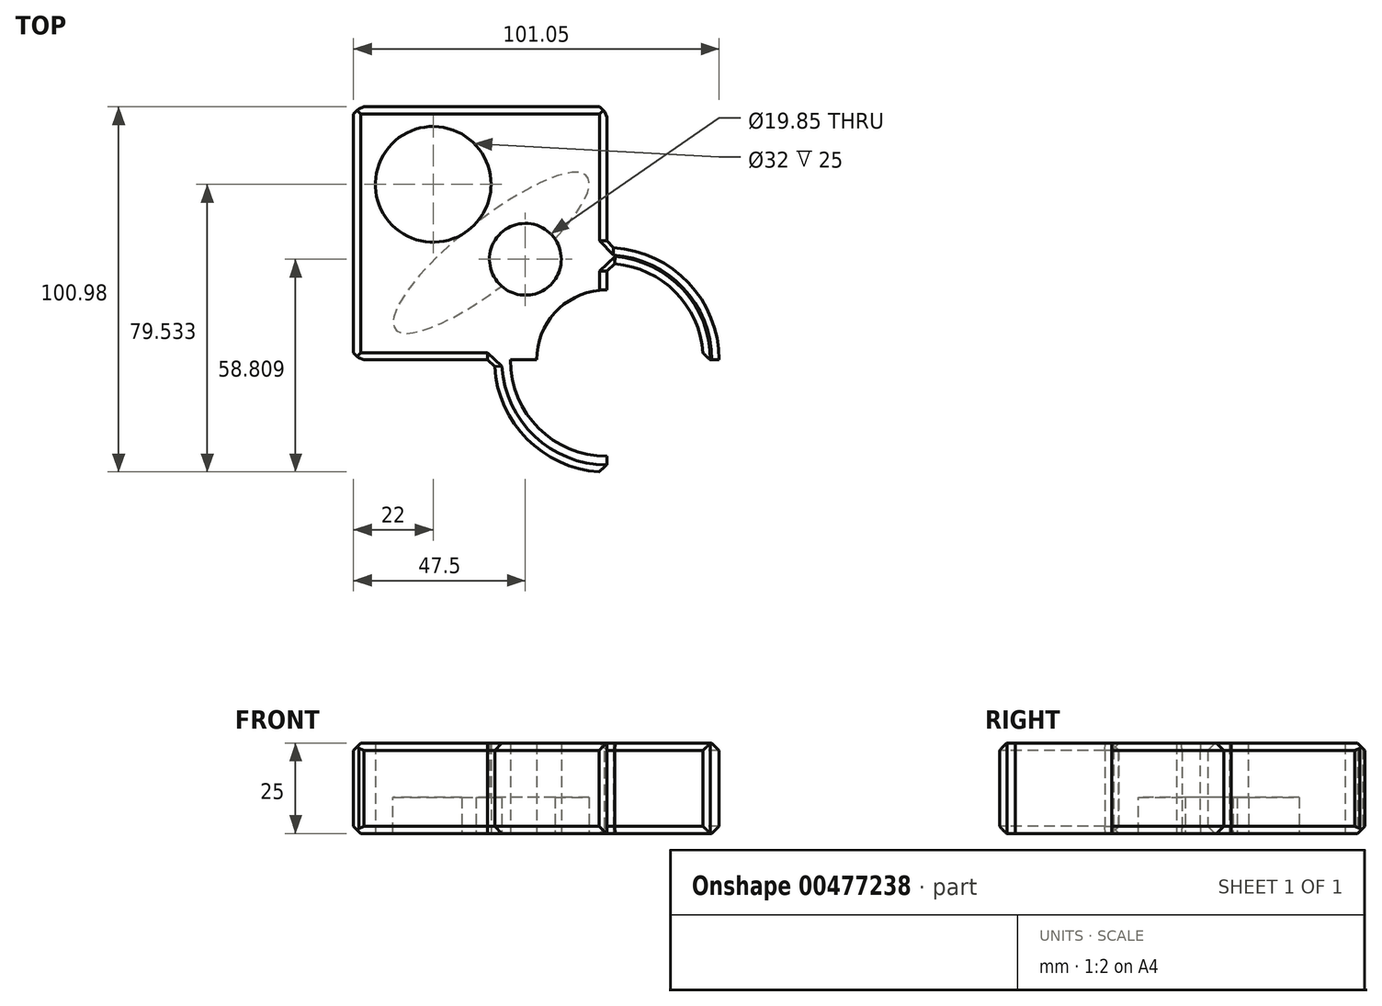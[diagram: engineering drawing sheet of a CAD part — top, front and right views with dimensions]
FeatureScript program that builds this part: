
annotation { "Feature Type Name" : "Feature", "Feature Type Description" : "" }
export const myFeature = defineFeature(function(context is Context, id is Id, definition is map)
    precondition{}
    {
        {
            var Q0;
            Q0=qCreatedBy(makeId("Top.planeOp"),FACE);
            var sketch = newSketch(context, id + "F0", { "sketchPlane" : qUnion([Q0])});
            skCircle(sketch, "E0", {"center": v(0, 0) * mm, "radius": 31.05 * mm});
            skSolve(sketch);
        }
        {
            var Q0;
            Q0=makeQuery(id+"F0.imprint","IMPRINT",FACE,{"disambiguationData":[TD([[makeQuery(id+"F0.imprint","IMPRINT",EDGE,{"derivedFrom":sQuery(id+"F0.wireOp",EDGE,"E0")}),1.0]])]});
            extrude(context, id + "F1", {"entities" : qUnion([Q0]), "depth" : 25 * mm});
        }
        {
            var Q0;
            Q0=qCreatedBy(makeId("Top.planeOp"),FACE);
            var sketch = newSketch(context, id + "F2", { "sketchPlane" : qUnion([Q0])});
            skCircle(sketch, "E1", {"center": v(0, 0) * mm, "radius": 26.67 * mm});
            skSolve(sketch);
        }
        {
            var Q0;
            Q0=makeQuery(id+"F2.imprint","IMPRINT",FACE,{"disambiguationData":[TD([[makeQuery(id+"F2.imprint","IMPRINT",EDGE,{"derivedFrom":sQuery(id+"F2.wireOp",EDGE,"E1")}),1.0]])]});
            extrude(context, id + "F3", {"entities" : qUnion([Q0]), "operationType" : NewBodyOperationType.REMOVE, "depth" : 25.2 * mm});
        }
        {
            var Q0;
            Q0=qCreatedBy(makeId("Top.planeOp"),FACE);
            var sketch = newSketch(context, id + "F4", { "sketchPlane" : qUnion([Q0])});
            skLineSegment(sketch, "E2.bottom", {"start": v(0, 0) * mm, "end": v(-70, 0) * mm});
            skLineSegment(sketch, "E2.top", {"start": v(0, 70) * mm, "end": v(-70, 70) * mm});
            skLineSegment(sketch, "E2.left", {"start": v(0, 0) * mm, "end": v(0, 70) * mm});
            skLineSegment(sketch, "E2.right", {"start": v(-70, 0) * mm, "end": v(-70, 70) * mm});
            skSolve(sketch);
        }
        {
            var Q0;
            Q0=qCreatedBy(makeId("Top.planeOp"),FACE);
            var sketch = newSketch(context, id + "F5", { "sketchPlane" : qUnion([Q0])});
            skLineSegment(sketch, "E3.bottom", {"start": v(70, -70) * mm, "end": v(0, -70) * mm});
            skLineSegment(sketch, "E3.top", {"start": v(70, 0) * mm, "end": v(0, 0) * mm});
            skLineSegment(sketch, "E3.left", {"start": v(70, -70) * mm, "end": v(70, 0) * mm});
            skLineSegment(sketch, "E3.right", {"start": v(0, -70) * mm, "end": v(0, 0) * mm});
            skSolve(sketch);
        }
        {
            var Q0;
            Q0=makeQuery(id+"F4.imprint","IMPRINT",FACE,{"disambiguationData":[TD([[makeQuery(id+"F4.imprint","IMPRINT",EDGE,{"derivedFrom":sQuery(id+"F4.wireOp",EDGE,"E2.bottom")}),-1.0]])]});
            extrude(context, id + "F6", {"entities" : qUnion([Q0]), "operationType" : NewBodyOperationType.ADD, "depth" : 25 * mm});
        }
        {
            var Q0;
            Q0=makeQuery(id+"F5.imprint","IMPRINT",FACE,{"disambiguationData":[TD([[makeQuery(id+"F5.imprint","IMPRINT",EDGE,{"derivedFrom":sQuery(id+"F5.wireOp",EDGE,"E3.bottom")}),-1.0]])]});
            extrude(context, id + "F7", {"entities" : qUnion([Q0]), "operationType" : NewBodyOperationType.REMOVE, "depth" : 25 * mm});
        }
        {
            var Q0;
            Q0=qCreatedBy(makeId("Top.planeOp"),FACE);
            var sketch = newSketch(context, id + "F8", { "sketchPlane" : qUnion([Q0])});
            skCircle(sketch, "E4", {"center": v(0, 0) * mm, "radius": 19.4 * mm});
            skSolve(sketch);
        }
        {
            var Q0;
            Q0 = qSketchRegion(id + "F8", true);
            extrude(context, id + "F9", {"entities" : qUnion([Q0]), "operationType" : NewBodyOperationType.REMOVE, "endBound" : BoundingType.THROUGH_ALL, "depth" : 25 * mm});
        }
        {
            var Q0;
            Q0=qCreatedBy(makeId("Top.planeOp"),FACE);
            var sketch = newSketch(context, id + "F10", { "sketchPlane" : qUnion([Q0])});
            skEllipse(sketch, "E5", {"center": v(-31.97, 29.6) * mm, "majorRadius": 33.9 * mm, "minorRadius": 9.04 * mm, "majorAxis": v(0.78, 0.62)});
            skSolve(sketch);
        }
        {
            var Q0;
            Q0 = qSketchRegion(id + "F10", true);
            extrude(context, id + "F11", {"entities" : qUnion([Q0]), "operationType" : NewBodyOperationType.REMOVE, "depth" : 10 * mm});
        }
        {
            var Q0;
            Q0=qCreatedBy(makeId("Top.planeOp"),FACE);
            var sketch = newSketch(context, id + "F12", { "sketchPlane" : qUnion([Q0])});
            skCircle(sketch, "E6", {"center": v(-22.5, 27.83) * mm, "radius": 9.93 * mm});
            skSolve(sketch);
        }
        {
            var Q0;
            Q0=makeQuery(id+"F12.imprint","IMPRINT",FACE,{"disambiguationData":[TD([[makeQuery(id+"F12.imprint","IMPRINT",EDGE,{"derivedFrom":sQuery(id+"F12.wireOp",EDGE,"E6")}),1.0]])]});
            var Q1;
            Q1=sQuery(id+"F12.wireOp",EDGE,"E6");
            extrude(context, id + "F13", {"entities" : qUnion([Q0]), "operationType" : NewBodyOperationType.REMOVE, "surfaceEntities" : qUnion([Q1]), "endBound" : BoundingType.THROUGH_ALL, "depth" : 25 * mm});
        }
        {
            var Q0;
            Q0=qCreatedBy(makeId("Top.planeOp"),FACE);
            var sketch = newSketch(context, id + "F14", { "sketchPlane" : qUnion([Q0])});
            skCircle(sketch, "E7", {"center": v(-48, 48.55) * mm, "radius": 16 * mm});
            skSolve(sketch);
        }
        {
            var Q0;
            Q0=makeQuery(id+"F14.imprint","IMPRINT",FACE,{"disambiguationData":[TD([[makeQuery(id+"F14.imprint","IMPRINT",EDGE,{"derivedFrom":sQuery(id+"F14.wireOp",EDGE,"E7")}),1.0]])]});
            var Q1;
            Q1=sQuery(id+"F14.wireOp",EDGE,"E7");
            extrude(context, id + "F15", {"entities" : qUnion([Q0]), "operationType" : NewBodyOperationType.REMOVE, "surfaceEntities" : qUnion([Q1]), "depth" : 25 * mm});
        }
        {
            var Q0;
            Q0=makeQuery(id+"F6.opExtrude","SWEPT_FACE",FACE,{"disambiguationData":[OSD([sQuery(id+"F4.wireOp",EDGE,"E2.right")])]});
            chamfer(context, id + "F16", {"entities" : qUnion([Q0]), "width" : 2 * mm, "tangentPropagation" : true});
        }
        {
            var Q0;
            Q0=makeQuery(id+"F6.opExtrude","SWEPT_FACE",FACE,{"disambiguationData":[OSD([sQuery(id+"F4.wireOp",EDGE,"E2.top")])]});
            chamfer(context, id + "F17", {"entities" : qUnion([Q0]), "width" : 2 * mm, "tangentPropagation" : true});
        }
        {
            var Q0;
            {var subQ0=sQuery(id+"F0.wireOp",EDGE,"E0");var subQ2=sQuery(id+"F4.wireOp",EDGE,"E2.left");Q0=makeQuery(id+"F6.boolean.opBoolean","SPLIT",FACE,{"disambiguationData":[TD([makeQuery(id+"F1.opExtrude","SWEPT_FACE",FACE,{"disambiguationData":[OSD([subQ0])]})])],"derivedFrom":makeQuery(id+"F6.opExtrude","SWEPT_FACE",FACE,{"disambiguationData":[OSD([subQ2])]})});}
            chamfer(context, id + "F18", {"entities" : qUnion([Q0]), "width" : 2 * mm, "tangentPropagation" : true});
        }
        {
            var Q0;
            {var subQ0=sQuery(id+"F0.wireOp",EDGE,"E0");var subQ4=sQuery(id+"F4.wireOp",EDGE,"E2.bottom");Q0=makeQuery(id+"F6.boolean.opBoolean","SPLIT",FACE,{"disambiguationData":[TD([makeQuery(id+"F1.opExtrude","SWEPT_FACE",FACE,{"disambiguationData":[OSD([subQ0])]})])],"derivedFrom":makeQuery(id+"F6.opExtrude","SWEPT_FACE",FACE,{"disambiguationData":[OSD([subQ4])]})});}
            var Q1;
            {var subQ1=sQuery(id+"F4.wireOp",EDGE,"E2.left");Q1=makeQuery(id+"F7.boolean.opBoolean","SPLIT",FACE,{"disambiguationData":[TD([makeQuery(id+"F6.opExtrude","SWEPT_FACE",FACE,{"disambiguationData":[OSD([subQ1])]})])],"derivedFrom":makeQuery(id+"F3.boolean.opBoolean","COPY",FACE,{"derivedFrom":makeQuery(id+"F3.opExtrude","SWEPT_FACE",FACE,{"disambiguationData":[OSD([sQuery(id+"F2.wireOp",EDGE,"E1")])]})})});}
            var Q2;
            {var subQ3=sQuery(id+"F4.wireOp",EDGE,"E2.bottom");var subQ4=sQuery(id+"F0.wireOp",EDGE,"E0");Q2=makeQuery(id+"F7.boolean.opBoolean","SPLIT",FACE,{"disambiguationData":[TD([makeQuery(id+"F6.opExtrude","SWEPT_FACE",FACE,{"disambiguationData":[OSD([subQ3])]})])],"derivedFrom":makeQuery(id+"F1.opExtrude","SWEPT_FACE",FACE,{"disambiguationData":[OSD([subQ4])]})});}
            chamfer(context, id + "F19", {"entities" : qUnion([Q0, Q1, Q2]), "width" : 2 * mm, "tangentPropagation" : true});
        }
    });
